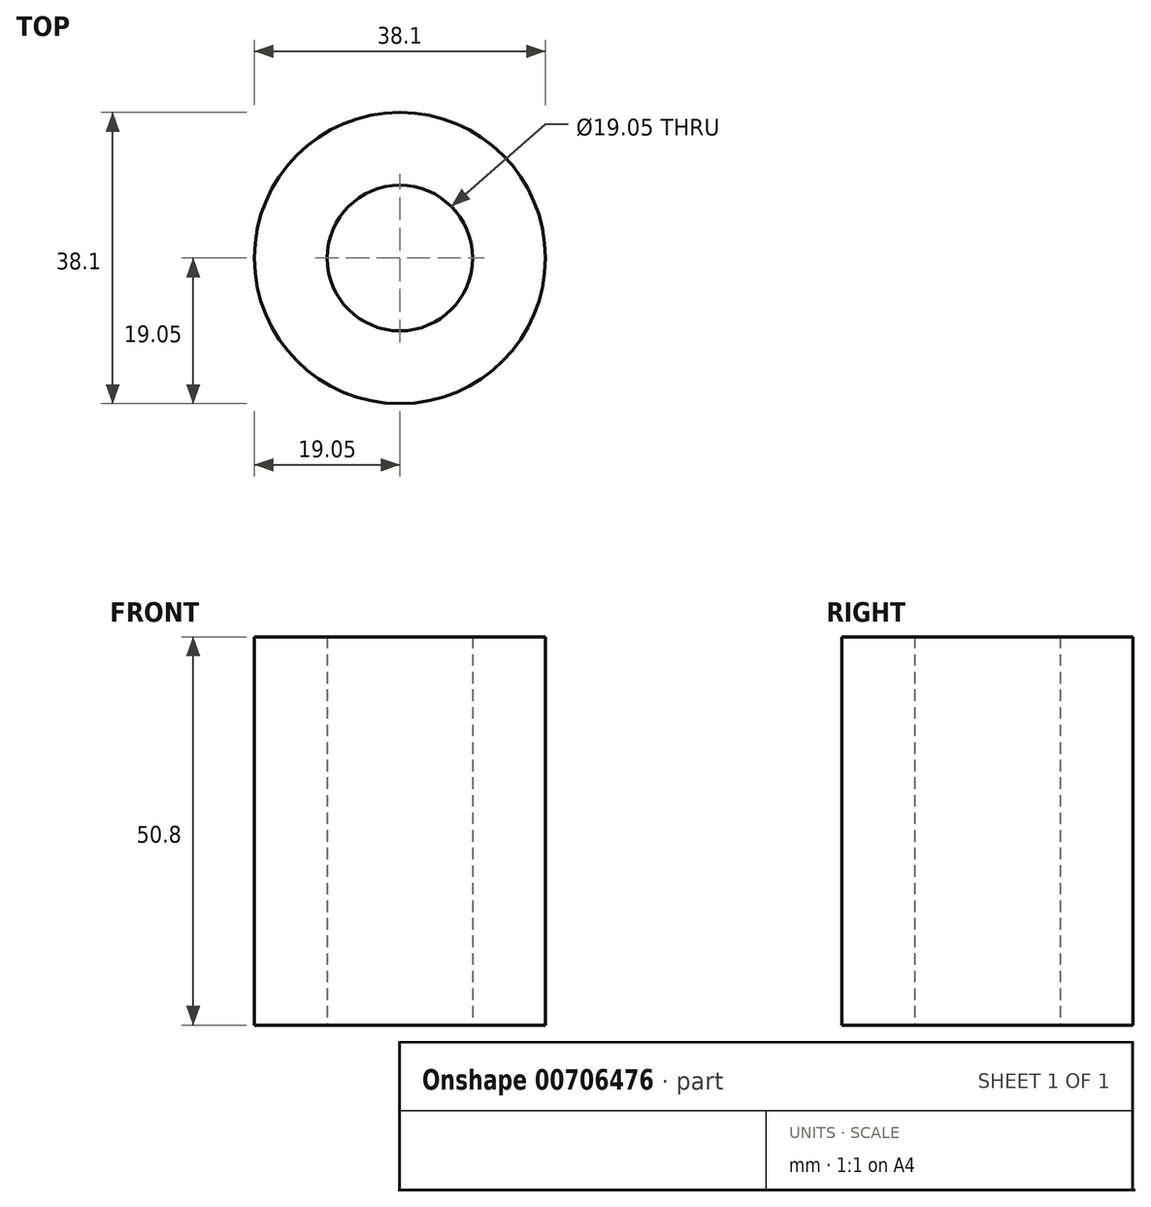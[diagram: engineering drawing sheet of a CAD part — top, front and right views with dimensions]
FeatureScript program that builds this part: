
annotation { "Feature Type Name" : "Feature", "Feature Type Description" : "" }
export const myFeature = defineFeature(function(context is Context, id is Id, definition is map)
    precondition{}
    {
        {
            var Q0;
            Q0=qCreatedBy(makeId("Top.planeOp"),FACE);
            var sketch = newSketch(context, id + "F0", { "sketchPlane" : qUnion([Q0])});
            skCircle(sketch, "E0", {"center": v(0, 0) * mm, "radius": 19.05 * mm});
            skCircle(sketch, "E1", {"center": v(0, 0) * mm, "radius": 9.53 * mm});
            skSolve(sketch);
        }
        {
            var Q0;
            Q0=makeQuery(id+"F0.imprint","IMPRINT",FACE,{"disambiguationData":[TD([[makeQuery(id+"F0.imprint","IMPRINT",EDGE,{"derivedFrom":sQuery(id+"F0.wireOp",EDGE,"E0")}),1.0]])]});
            extrude(context, id + "F1", {"entities" : qUnion([Q0]), "depth" : 50.8 * mm, "offsetDistance" : 25.4 * mm});
        }
    });
